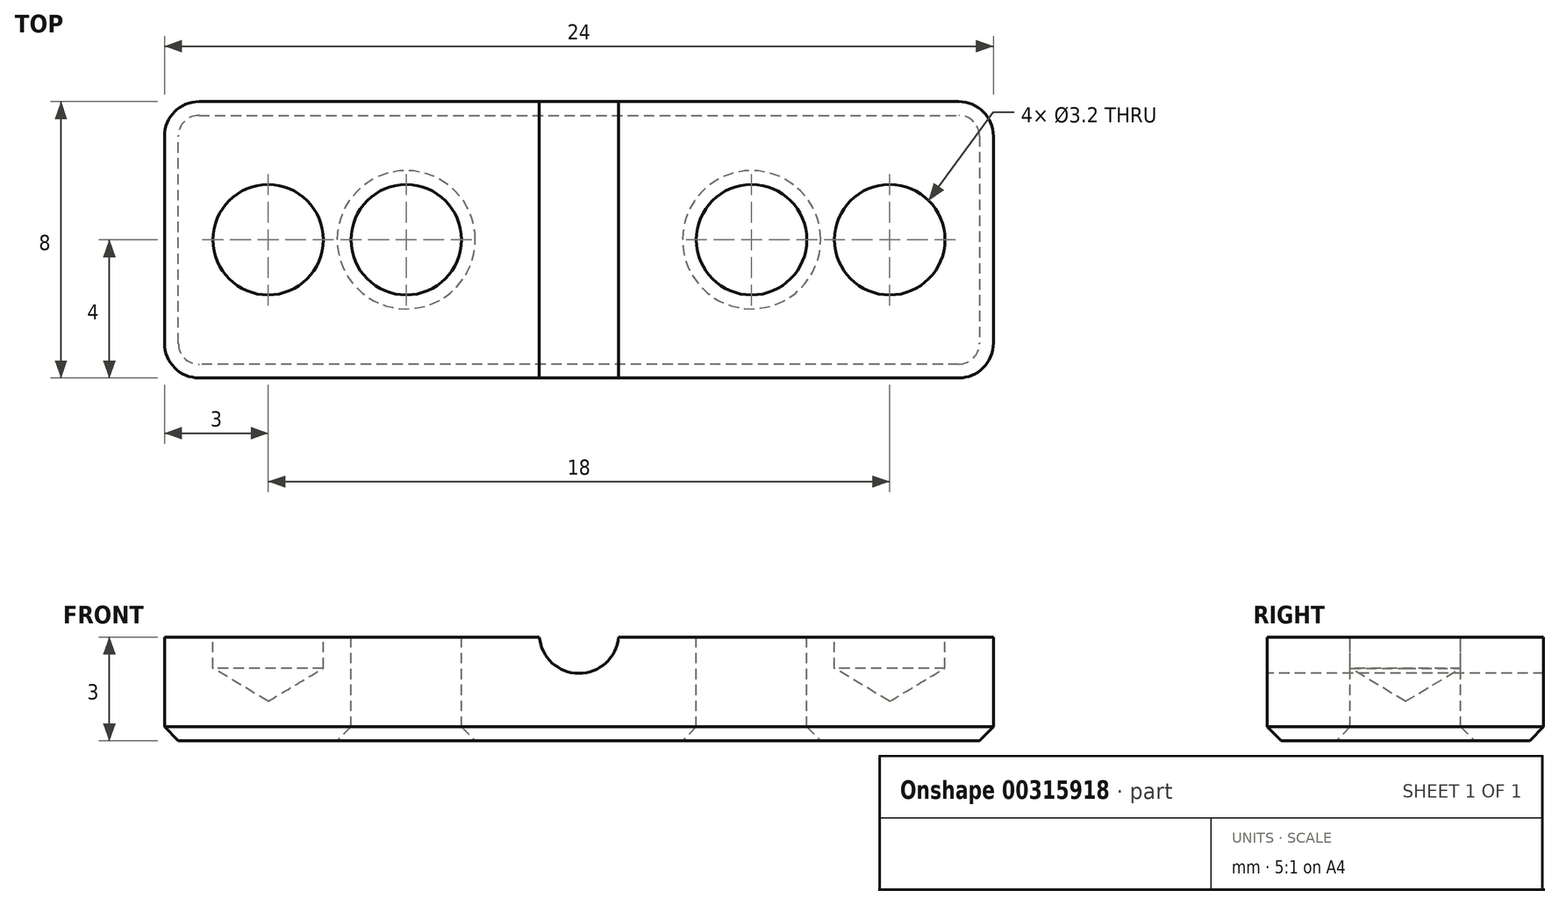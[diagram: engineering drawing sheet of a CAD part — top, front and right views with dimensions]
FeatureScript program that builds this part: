
annotation { "Feature Type Name" : "Feature", "Feature Type Description" : "" }
export const myFeature = defineFeature(function(context is Context, id is Id, definition is map)
    precondition{}
    {
        {
            var Q0;
            Q0=qCreatedBy(makeId("Top.planeOp"),FACE);
            var sketch = newSketch(context, id + "F0", { "sketchPlane" : qUnion([Q0])});
            skLineSegment(sketch, "E0.bottom", {"start": v(3, 4) * mm, "end": v(-3, 4) * mm});
            skLineSegment(sketch, "E0.top", {"start": v(3, -4) * mm, "end": v(-3, -4) * mm});
            skLineSegment(sketch, "E0.left", {"start": v(3, 4) * mm, "end": v(3, -4) * mm});
            skLineSegment(sketch, "E0.right", {"start": v(-3, 4) * mm, "end": v(-3, -4) * mm});
            skPoint(sketch, "E0.middle", {"position": v(0, 0) * mm});
            skLineSegment(sketch, "E1.bottom", {"start": v(21, 4) * mm, "end": v(15, 4) * mm});
            skLineSegment(sketch, "E1.top", {"start": v(21, -4) * mm, "end": v(15, -4) * mm});
            skLineSegment(sketch, "E1.left", {"start": v(21, 4) * mm, "end": v(21, -4) * mm});
            skLineSegment(sketch, "E1.right", {"start": v(15, 4) * mm, "end": v(15, -4) * mm});
            skPoint(sketch, "E1.middle", {"position": v(18, 0) * mm});
            skLineSegment(sketch, "E2", {"start": v(3, 4) * mm, "end": v(15, 4) * mm});
            skLineSegment(sketch, "E3", {"start": v(3, -4) * mm, "end": v(15, -4) * mm});
            skLineSegment(sketch, "E4", {"start": v(9, 4) * mm, "end": v(9, -4) * mm, "construction": true});
            skLineSegment(sketch, "E5.direction1", {"start": v(9, -4) * mm, "end": v(15, -4) * mm, "construction": true});
            skPoint(sketch, "E6", {"position": v(4, 0) * mm});
            skPoint(sketch, "E6.positionSnap0", {"position": v(3, 0) * mm});
            skPoint(sketch, "E7", {"position": v(14, 0) * mm});
            skPoint(sketch, "E7.positionSnap0", {"position": v(15, 0) * mm});
            skSolve(sketch);
        }
        {
            var Q0;
            Q0=makeQuery(id+"F0.imprint","IMPRINT",FACE,{"disambiguationData":[TD([[makeQuery(id+"F0.imprint","IMPRINT",EDGE,{"derivedFrom":sQuery(id+"F0.wireOp",EDGE,"E0.bottom")}),1.0]])]});
            var Q1;
            Q1=makeQuery(id+"F0.imprint","IMPRINT",FACE,{"disambiguationData":[TD([[makeQuery(id+"F0.imprint","IMPRINT",EDGE,{"derivedFrom":sQuery(id+"F0.wireOp",EDGE,"E0.left")}),1.0]])]});
            var Q2;
            Q2=makeQuery(id+"F0.imprint","IMPRINT",FACE,{"disambiguationData":[TD([[makeQuery(id+"F0.imprint","IMPRINT",EDGE,{"derivedFrom":sQuery(id+"F0.wireOp",EDGE,"E1.bottom")}),1.0]])]});
            extrude(context, id + "F1", {"entities" : qUnion([Q0, Q1, Q2]), "oppositeDirection" : true, "depth" : 3.1 * mm});
        }
        {
            var Q0;
            Q0=sQuery(id+"F0.wireOp",VERTEX,"E6");
            var Q1;
            Q1=sQuery(id+"F0.wireOp",VERTEX,"E7");
            var Q2;
            Q2=makeQuery(id+"F1.opExtrude","SWEPT_BODY",BODY,{"disambiguationData":[OSD([sQuery(id+"F0.wireOp",EDGE,"E0.bottom"),sQuery(id+"F0.wireOp",EDGE,"E0.top"),sQuery(id+"F0.wireOp",EDGE,"E0.right"),sQuery(id+"F0.wireOp",EDGE,"E1.bottom"),sQuery(id+"F0.wireOp",EDGE,"E1.top"),sQuery(id+"F0.wireOp",EDGE,"E1.left"),sQuery(id+"F0.wireOp",EDGE,"E2"),sQuery(id+"F0.wireOp",EDGE,"E3")])]});
            hole(context, id + "F2", {"style" : HoleStyle.SIMPLE, "endStyle" : HoleEndStyle.THROUGH, "holeDiameter" : 3.2 * mm, "tappedDepth" : 12 * mm, "tapClearance" : 3, "locations" : qUnion([Q0, Q1]), "scope" : qUnion([Q2])});
        }
        {
            var Q0;
            Q0=sQuery(id+"F0.wireOp",VERTEX,"E0.middle");
            var Q1;
            Q1=sQuery(id+"F0.wireOp",VERTEX,"E1.middle");
            var Q2;
            Q2=makeQuery(id+"F1.opExtrude","SWEPT_BODY",BODY,{"disambiguationData":[OSD([sQuery(id+"F0.wireOp",EDGE,"E0.bottom"),sQuery(id+"F0.wireOp",EDGE,"E0.top"),sQuery(id+"F0.wireOp",EDGE,"E0.right"),sQuery(id+"F0.wireOp",EDGE,"E1.bottom"),sQuery(id+"F0.wireOp",EDGE,"E1.top"),sQuery(id+"F0.wireOp",EDGE,"E1.left"),sQuery(id+"F0.wireOp",EDGE,"E2"),sQuery(id+"F0.wireOp",EDGE,"E3")])]});
            hole(context, id + "F3", {"style" : HoleStyle.SIMPLE, "endStyle" : HoleEndStyle.BLIND, "holeDiameter" : 3.2 * mm, "holeDepth" : 1 * mm, "tappedDepth" : 12 * mm, "tapClearance" : 3, "locations" : qUnion([Q0, Q1]), "scope" : qUnion([Q2])});
        }
        {
            var Q0;
            {var subQ0=sQuery(id+"F0.wireOp",EDGE,"E3");var subQ1=sQuery(id+"F0.wireOp",EDGE,"E1.top");var subQ2=sQuery(id+"F0.wireOp",EDGE,"E0.top");Q0=makeQuery(id+"FaaVOSY5iOmgxNq_1.boolean.opBoolean","MERGE",FACE,{"derivedFrom":[makeQuery(id+"F1.opExtrude","SWEPT_FACE",FACE,{"disambiguationData":[OSD([subQ2,subQ1,subQ0])]}),makeQuery(id+"FaaVOSY5iOmgxNq_1.opExtrude","SWEPT_FACE",FACE,{"disambiguationData":[OSD([subQ2,subQ1,subQ0])]})]});}
            var sketch = newSketch(context, id + "F4", { "sketchPlane" : qUnion([Q0])});
            skPoint(sketch, "E8", {"position": v(9, 0) * mm});
            skPoint(sketch, "E9.1.0.0", {"position": v(15, 0) * mm});
            skLineSegment(sketch, "E9.direction1", {"start": v(9, 0) * mm, "end": v(15, 0) * mm, "construction": true});
            skSolve(sketch);
        }
        {
            var Q0;
            Q0=sQuery(id+"F4.wireOp",VERTEX,"E8");
            var Q1;
            Q1=makeQuery(id+"F1.opExtrude","SWEPT_BODY",BODY,{"disambiguationData":[OSD([sQuery(id+"F0.wireOp",EDGE,"E0.bottom"),sQuery(id+"F0.wireOp",EDGE,"E0.top"),sQuery(id+"F0.wireOp",EDGE,"E0.right"),sQuery(id+"F0.wireOp",EDGE,"E1.bottom"),sQuery(id+"F0.wireOp",EDGE,"E1.top"),sQuery(id+"F0.wireOp",EDGE,"E1.left"),sQuery(id+"F0.wireOp",EDGE,"E2"),sQuery(id+"F0.wireOp",EDGE,"E3")])]});
            hole(context, id + "F5", {"style" : HoleStyle.SIMPLE, "endStyle" : HoleEndStyle.THROUGH, "holeDiameter" : 2.3 * mm, "tappedDepth" : 12 * mm, "tapClearance" : 3, "locations" : qUnion([Q0]), "scope" : qUnion([Q1])});
        }
        {
            var Q0;
            Q0=makeQuery(id+"F1.opExtrude","SWEPT_EDGE",EDGE,{"disambiguationData":[OSD([sQuery(id+"F0.wireOp",EDGE,"E0.top"),sQuery(id+"F0.wireOp",EDGE,"E0.right")])]});
            var Q1;
            Q1=makeQuery(id+"F1.opExtrude","SWEPT_EDGE",EDGE,{"disambiguationData":[OSD([sQuery(id+"F0.wireOp",EDGE,"E1.top"),sQuery(id+"F0.wireOp",EDGE,"E1.left")])]});
            var Q2;
            Q2=makeQuery(id+"F1.opExtrude","SWEPT_EDGE",EDGE,{"disambiguationData":[OSD([sQuery(id+"F0.wireOp",EDGE,"E1.bottom"),sQuery(id+"F0.wireOp",EDGE,"E1.left")])]});
            var Q3;
            Q3=makeQuery(id+"F1.opExtrude","SWEPT_EDGE",EDGE,{"disambiguationData":[OSD([sQuery(id+"F0.wireOp",EDGE,"E0.bottom"),sQuery(id+"F0.wireOp",EDGE,"E0.right")])]});
            fillet(context, id + "F6", {"entities" : qUnion([Q0, Q1, Q2, Q3]), "radius" : 1 * mm, "tangentPropagation" : true, "allowEdgeOverflow" : false});
        }
        {
            var Q0;
            Q0=makeQuery(id+"F1.opExtrude","CAP_FACE",FACE,{"disambiguationData":[OSD([sQuery(id+"F0.wireOp",EDGE,"E0.bottom"),sQuery(id+"F0.wireOp",EDGE,"E0.top"),sQuery(id+"F0.wireOp",EDGE,"E0.right"),sQuery(id+"F0.wireOp",EDGE,"E1.bottom"),sQuery(id+"F0.wireOp",EDGE,"E1.top"),sQuery(id+"F0.wireOp",EDGE,"E1.left"),sQuery(id+"F0.wireOp",EDGE,"E2"),sQuery(id+"F0.wireOp",EDGE,"E3")])],"isStart":false});
            chamfer(context, id + "F7", {"entities" : qUnion([Q0]), "width" : 0.4 * mm, "tangentPropagation" : true});
        }
        {
            var Q0;
            {var subQ0=sQuery(id+"F0.wireOp",EDGE,"E0.right");var subQ1=sQuery(id+"F0.wireOp",EDGE,"E3");var subQ2=sQuery(id+"F0.wireOp",EDGE,"E1.top");var subQ3=sQuery(id+"F0.wireOp",EDGE,"E0.top");var subQ4=sQuery(id+"F0.wireOp",EDGE,"E2");var subQ5=sQuery(id+"F0.wireOp",EDGE,"E1.bottom");var subQ6=sQuery(id+"F0.wireOp",EDGE,"E0.bottom");Q0=makeQuery(id+"F5.hole-0.boolean.opBoolean","SPLIT",FACE,{"disambiguationData":[TD([makeQuery(id+"F1.opExtrude","SWEPT_FACE",FACE,{"disambiguationData":[OSD([subQ0])]})])],"derivedFrom":makeQuery(id+"F1.opExtrude","CAP_FACE",FACE,{"disambiguationData":[OSD([subQ6,subQ3,subQ0,subQ5,subQ2,sQuery(id+"F0.wireOp",EDGE,"E1.left"),subQ4,subQ1])],"isStart":true})});}
            var Q1;
            {var subQ0=sQuery(id+"F0.wireOp",EDGE,"E2");var subQ1=sQuery(id+"F0.wireOp",EDGE,"E1.bottom");var subQ2=sQuery(id+"F0.wireOp",EDGE,"E0.bottom");var subQ4=sQuery(id+"F0.wireOp",EDGE,"E3");var subQ5=sQuery(id+"F0.wireOp",EDGE,"E1.top");var subQ6=sQuery(id+"F0.wireOp",EDGE,"E0.top");var subQ8=makeQuery(id+"F5.hole-0.opRevolve","SWEPT_FACE",FACE,{"disambiguationData":[OSD([sQuery(id+"F5.hole-0.sketch.wireOp",EDGE,"core_line_2")])]});var subQ9=makeQuery(id+"F5.hole-0.boolean.opBoolean","COPY",FACE,{"derivedFrom":subQ8});var subQ10=sQuery(id+"F0.wireOp",EDGE,"E1.left");Q1=makeQuery(id+"F5.hole-2.boolean.opBoolean","SPLIT",FACE,{"disambiguationData":[TD([subQ9])],"derivedFrom":makeQuery(id+"F5.hole-1.boolean.opBoolean","SPLIT",FACE,{"disambiguationData":[TD([subQ9])],"derivedFrom":makeQuery(id+"F5.hole-0.boolean.opBoolean","SPLIT",FACE,{"disambiguationData":[TD([makeQuery(id+"F1.opExtrude","SWEPT_FACE",FACE,{"disambiguationData":[OSD([subQ10])]})])],"derivedFrom":makeQuery(id+"F1.opExtrude","CAP_FACE",FACE,{"disambiguationData":[OSD([subQ2,subQ6,sQuery(id+"F0.wireOp",EDGE,"E0.right"),subQ1,subQ5,subQ10,subQ0,subQ4])],"isStart":true})})})});}
            var Q2;
            {var subQ0=sQuery(id+"F0.wireOp",EDGE,"E2");var subQ1=sQuery(id+"F0.wireOp",EDGE,"E1.bottom");var subQ2=sQuery(id+"F0.wireOp",EDGE,"E0.bottom");var subQ4=sQuery(id+"F0.wireOp",EDGE,"E3");var subQ5=sQuery(id+"F0.wireOp",EDGE,"E1.top");var subQ6=sQuery(id+"F0.wireOp",EDGE,"E0.top");var subQ8=makeQuery(id+"F5.hole-1.opRevolve","SWEPT_FACE",FACE,{"disambiguationData":[OSD([sQuery(id+"F5.hole-1.sketch.wireOp",EDGE,"core_line_2")])]});var subQ9=makeQuery(id+"F5.hole-0.opRevolve","SWEPT_FACE",FACE,{"disambiguationData":[OSD([sQuery(id+"F5.hole-0.sketch.wireOp",EDGE,"core_line_2")])]});var subQ10=sQuery(id+"F0.wireOp",EDGE,"E1.left");Q2=makeQuery(id+"F5.hole-2.boolean.opBoolean","SPLIT",FACE,{"disambiguationData":[TD([makeQuery(id+"F5.hole-1.boolean.opBoolean","COPY",FACE,{"derivedFrom":subQ8})])],"derivedFrom":makeQuery(id+"F5.hole-1.boolean.opBoolean","SPLIT",FACE,{"disambiguationData":[TD([makeQuery(id+"F5.hole-0.boolean.opBoolean","COPY",FACE,{"derivedFrom":subQ9})])],"derivedFrom":makeQuery(id+"F5.hole-0.boolean.opBoolean","SPLIT",FACE,{"disambiguationData":[TD([makeQuery(id+"F1.opExtrude","SWEPT_FACE",FACE,{"disambiguationData":[OSD([subQ10])]})])],"derivedFrom":makeQuery(id+"F1.opExtrude","CAP_FACE",FACE,{"disambiguationData":[OSD([subQ2,subQ6,sQuery(id+"F0.wireOp",EDGE,"E0.right"),subQ1,subQ5,subQ10,subQ0,subQ4])],"isStart":true})})})});}
            var Q3;
            {var subQ1=sQuery(id+"F0.wireOp",EDGE,"E3");var subQ2=sQuery(id+"F0.wireOp",EDGE,"E1.top");var subQ3=sQuery(id+"F0.wireOp",EDGE,"E0.top");var subQ5=sQuery(id+"F0.wireOp",EDGE,"E1.left");var subQ6=makeQuery(id+"F1.opExtrude","SWEPT_FACE",FACE,{"disambiguationData":[OSD([subQ5])]});var subQ7=sQuery(id+"F0.wireOp",EDGE,"E2");var subQ8=sQuery(id+"F0.wireOp",EDGE,"E1.bottom");var subQ9=sQuery(id+"F0.wireOp",EDGE,"E0.bottom");Q3=makeQuery(id+"F5.hole-1.boolean.opBoolean","SPLIT",FACE,{"disambiguationData":[TD([subQ6])],"derivedFrom":makeQuery(id+"F5.hole-0.boolean.opBoolean","SPLIT",FACE,{"disambiguationData":[TD([subQ6])],"derivedFrom":makeQuery(id+"F1.opExtrude","CAP_FACE",FACE,{"disambiguationData":[OSD([subQ9,subQ3,sQuery(id+"F0.wireOp",EDGE,"E0.right"),subQ8,subQ2,subQ5,subQ7,subQ1])],"isStart":true})})});}
            extrude(context, id + "F8", {"entities" : qUnion([Q0, Q1, Q2, Q3]), "operationType" : NewBodyOperationType.REMOVE, "oppositeDirection" : true, "depth" : 0.1 * mm});
        }
    });
